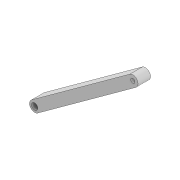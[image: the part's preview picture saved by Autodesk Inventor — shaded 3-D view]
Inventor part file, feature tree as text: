
AUTODESK INVENTOR PART (.ipt)
format: ipt  version: 2020.3 (Build 243373010, 373A)  size: 82,432 bytes
history: native  units: mm
features: extrude x1, sketch x1
ambient origin geometry x8: Origin, YZ Plane, XZ Plane, XY Plane, X Axis, Y Axis, Z Axis, Center Point
bodies: Solid1 (feature_tree)
feature tree (2):
  extrude  "Extrusion1"  Depth=24.0mm TaperAngle=0.0deg
  sketch  "Sketch1"  dims[d0=8.0mm d1=24.0mm d2=0.0mm d3=12.0mm]
